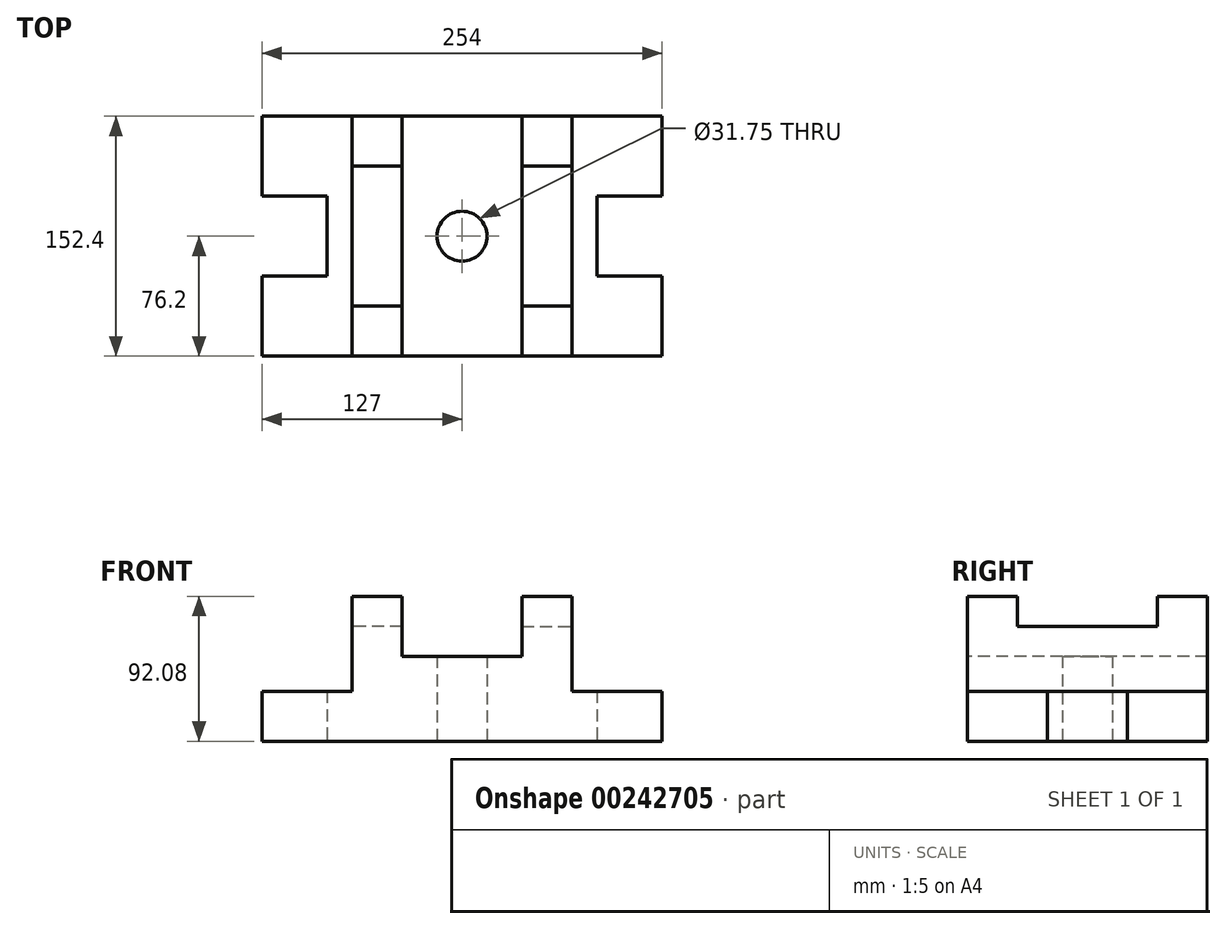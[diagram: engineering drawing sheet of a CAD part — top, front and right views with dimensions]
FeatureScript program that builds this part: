
annotation { "Feature Type Name" : "Feature", "Feature Type Description" : "" }
export const myFeature = defineFeature(function(context is Context, id is Id, definition is map)
    precondition{}
    {
        {
            var Q0;
            Q0=qCreatedBy(makeId("Top.planeOp"),FACE);
            var sketch = newSketch(context, id + "F0", { "sketchPlane" : qUnion([Q0])});
            skLineSegment(sketch, "E0.bottom", {"start": v(127, 76.2) * mm, "end": v(-127, 76.2) * mm});
            skLineSegment(sketch, "E0.top", {"start": v(127, -76.2) * mm, "end": v(-127, -76.2) * mm});
            skLineSegment(sketch, "E0.left", {"start": v(127, 76.2) * mm, "end": v(127, 25.4) * mm});
            skLineSegment(sketch, "E0.right", {"start": v(-127, 76.2) * mm, "end": v(-127, 25.4) * mm});
            skPoint(sketch, "E0.middle", {"position": v(0, 0) * mm});
            skLineSegment(sketch, "E1.bottom", {"start": v(127, -25.4) * mm, "end": v(85.72, -25.4) * mm});
            skLineSegment(sketch, "E1.top", {"start": v(127, 25.4) * mm, "end": v(85.72, 25.4) * mm});
            skLineSegment(sketch, "E1.right", {"start": v(85.72, -25.4) * mm, "end": v(85.72, 25.4) * mm});
            skLineSegment(sketch, "E2", {"start": v(69.85, -76.2) * mm, "end": v(69.85, 76.2) * mm});
            skLineSegment(sketch, "E3", {"start": v(38.1, 76.2) * mm, "end": v(38.1, -76.2) * mm});
            skLineSegment(sketch, "E4", {"start": v(38.1, 44.45) * mm, "end": v(69.85, 44.45) * mm});
            skLineSegment(sketch, "E5", {"start": v(69.85, 44.45) * mm, "end": v(69.85, -44.45) * mm});
            skLineSegment(sketch, "E6", {"start": v(69.85, -44.45) * mm, "end": v(38.1, -44.45) * mm});
            skLineSegment(sketch, "E7", {"start": v(-38.1, 76.2) * mm, "end": v(-38.1, -76.2) * mm});
            skLineSegment(sketch, "E8", {"start": v(-69.85, 76.2) * mm, "end": v(-69.85, -76.2) * mm});
            skLineSegment(sketch, "E9", {"start": v(-38.1, 44.45) * mm, "end": v(-69.85, 44.45) * mm});
            skLineSegment(sketch, "E10", {"start": v(-38.1, -44.45) * mm, "end": v(-69.85, -44.45) * mm});
            skLineSegment(sketch, "E11.bottom", {"start": v(-127, 25.4) * mm, "end": v(-85.72, 25.4) * mm});
            skLineSegment(sketch, "E11.top", {"start": v(-127, -25.4) * mm, "end": v(-85.72, -25.4) * mm});
            skLineSegment(sketch, "E11.right", {"start": v(-85.72, 25.4) * mm, "end": v(-85.72, -25.4) * mm});
            skCircle(sketch, "E12", {"center": v(0, 0) * mm, "radius": 15.88 * mm});
            skLineSegment(sketch, "E13.trimOffspring", {"start": v(-127, -25.4) * mm, "end": v(-127, -76.2) * mm});
            skLineSegment(sketch, "E14.trimOffspring", {"start": v(127, -25.4) * mm, "end": v(127, -76.2) * mm});
            skSolve(sketch);
        }
        {
            var Q0;
            {var subQ5=sQuery(id+"F0.wireOp",EDGE,"E10");Q0=makeQuery(id+"F0.imprint","IMPRINT",FACE,{"disambiguationData":[TD([[makeQuery(id+"F0.imprint","IMPRINT",EDGE,{"derivedFrom":subQ5}),1.0]])]});}
            var Q1;
            {var subQ5=sQuery(id+"F0.wireOp",EDGE,"E9");Q1=makeQuery(id+"F0.imprint","IMPRINT",FACE,{"disambiguationData":[TD([[makeQuery(id+"F0.imprint","IMPRINT",EDGE,{"derivedFrom":subQ5}),-1.0]])]});}
            var Q2;
            {var subQ5=sQuery(id+"F0.wireOp",EDGE,"E4");Q2=makeQuery(id+"F0.imprint","IMPRINT",FACE,{"disambiguationData":[TD([[makeQuery(id+"F0.imprint","IMPRINT",EDGE,{"derivedFrom":subQ5}),1.0]])]});}
            var Q3;
            {var subQ5=sQuery(id+"F0.wireOp",EDGE,"E6");Q3=makeQuery(id+"F0.imprint","IMPRINT",FACE,{"disambiguationData":[TD([[makeQuery(id+"F0.imprint","IMPRINT",EDGE,{"derivedFrom":subQ5}),1.0]])]});}
            extrude(context, id + "F1", {"entities" : qUnion([Q0, Q1, Q2, Q3]), "depth" : 92.07 * mm});
        }
        {
            var Q0;
            {var subQ10=sQuery(id+"F0.wireOp",EDGE,"E11.bottom");Q0=makeQuery(id+"F0.imprint","IMPRINT",FACE,{"disambiguationData":[TD([[makeQuery(id+"F0.imprint","IMPRINT",EDGE,{"derivedFrom":subQ10}),1.0]])]});}
            var Q1;
            {var subQ4=sQuery(id+"F0.wireOp",EDGE,"E1.bottom");Q1=makeQuery(id+"F0.imprint","IMPRINT",FACE,{"disambiguationData":[TD([[makeQuery(id+"F0.imprint","IMPRINT",EDGE,{"derivedFrom":subQ4}),1.0]])]});}
            extrude(context, id + "F2", {"entities" : qUnion([Q0, Q1]), "operationType" : NewBodyOperationType.ADD, "depth" : 31.75 * mm});
        }
        {
            var Q0;
            {var subQ0=sQuery(id+"F0.wireOp",EDGE,"E9");Q0=makeQuery(id+"F0.imprint","IMPRINT",FACE,{"disambiguationData":[TD([[makeQuery(id+"F0.imprint","IMPRINT",EDGE,{"derivedFrom":subQ0}),1.0]])]});}
            var Q1;
            {var subQ0=sQuery(id+"F0.wireOp",EDGE,"E4");Q1=makeQuery(id+"F0.imprint","IMPRINT",FACE,{"disambiguationData":[TD([[makeQuery(id+"F0.imprint","IMPRINT",EDGE,{"derivedFrom":subQ0}),-1.0]])]});}
            extrude(context, id + "F3", {"entities" : qUnion([Q0, Q1]), "operationType" : NewBodyOperationType.ADD, "depth" : 73.02 * mm});
        }
        {
            var Q0;
            {var subQ0=sQuery(id+"F0.wireOp",EDGE,"E3");var subQ7=sQuery(id+"F0.wireOp",EDGE,"E0.bottom");var subQ8=makeQuery(id+"F0.imprint","INTERSECT",VERTEX,{"derivedFrom":[subQ7,subQ0]});Q0=makeQuery(id+"F0.imprint","IMPRINT",FACE,{"disambiguationData":[TD([[makeQuery(id+"F0.imprint","IMPRINT",EDGE,{"disambiguationData":[TD([[subQ8,-1.0]])],"derivedFrom":subQ7}),1.0]])]});}
            extrude(context, id + "F4", {"entities" : qUnion([Q0]), "operationType" : NewBodyOperationType.ADD, "depth" : 53.97 * mm});
        }
    });
